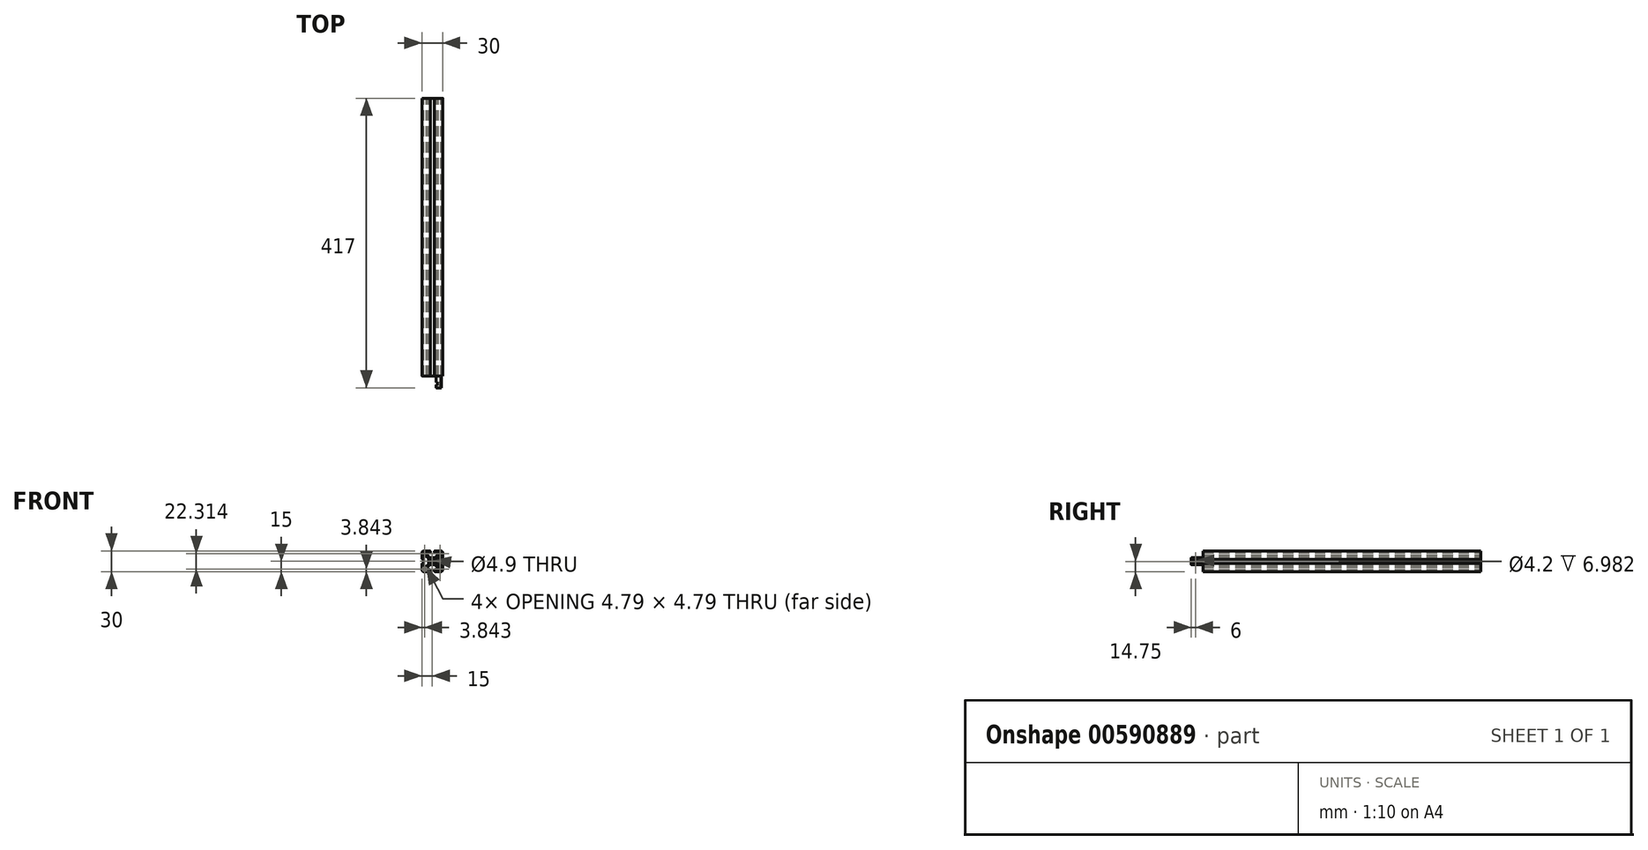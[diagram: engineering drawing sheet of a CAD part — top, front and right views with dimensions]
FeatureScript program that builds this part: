
annotation { "Feature Type Name" : "Feature", "Feature Type Description" : "" }
export const myFeature = defineFeature(function(context is Context, id is Id, definition is map)
    precondition{}
    {
        {
            var Q0;
            Q0=qCreatedBy(makeId("Front.planeOp"),FACE);
            var sketch = newSketch(context, id + "F0", { "sketchPlane" : qUnion([Q0])});
            skPoint(sketch, "E0.middle", {"position": v(0, 0) * mm});
            skCircle(sketch, "E1", {"center": v(0, 0) * mm, "radius": 2.45 * mm});
            skLineSegment(sketch, "E2", {"start": v(15, -15) * mm, "end": v(15, -3) * mm});
            skLineSegment(sketch, "E3", {"start": v(15, -3) * mm, "end": v(12.1, -3) * mm});
            skLineSegment(sketch, "E4", {"start": v(12.1, -3) * mm, "end": v(12.1, -5.9) * mm});
            skLineSegment(sketch, "E5", {"start": v(12.1, -5.9) * mm, "end": v(13.55, -5.9) * mm});
            skLineSegment(sketch, "E6", {"start": v(13.55, -5.9) * mm, "end": v(13.55, -7.35) * mm});
            skLineSegment(sketch, "E7", {"start": v(13.55, -7.35) * mm, "end": v(8.76, -7.35) * mm});
            skLineSegment(sketch, "E8", {"start": v(8.76, -7.35) * mm, "end": v(5.1, -3.69) * mm});
            skLineSegment(sketch, "E9", {"start": v(5.1, -3.69) * mm, "end": v(5.1, 0) * mm});
            skLineSegment(sketch, "E10", {"start": v(-37.03, 0) * mm, "end": v(41.88, 0) * mm, "construction": true});
            skLineSegment(sketch, "E11", {"start": v(0, 0) * mm, "end": v(18.28, -18.28) * mm, "construction": true});
            skLineSegment(sketch, "E12.MirrorCS", {"start": v(3.69, -5.1) * mm, "end": v(0, -5.1) * mm});
            skLineSegment(sketch, "E13.MirrorCS", {"start": v(7.35, -8.76) * mm, "end": v(3.69, -5.1) * mm});
            skLineSegment(sketch, "E14.MirrorCS", {"start": v(7.35, -13.55) * mm, "end": v(7.35, -8.76) * mm});
            skLineSegment(sketch, "E15.MirrorCS", {"start": v(5.9, -13.55) * mm, "end": v(7.35, -13.55) * mm});
            skLineSegment(sketch, "E16.MirrorCS", {"start": v(5.9, -12.1) * mm, "end": v(5.9, -13.55) * mm});
            skLineSegment(sketch, "E17.MirrorCS", {"start": v(3, -12.1) * mm, "end": v(5.9, -12.1) * mm});
            skLineSegment(sketch, "E18.MirrorCS", {"start": v(3, -15) * mm, "end": v(3, -12.1) * mm});
            skLineSegment(sketch, "E19.MirrorCS", {"start": v(15, -15) * mm, "end": v(3, -15) * mm});
            skLineSegment(sketch, "E20", {"start": v(0, 28.81) * mm, "end": v(0, -46.75) * mm, "construction": true});
            skLineSegment(sketch, "E21.MirrorCS", {"start": v(-5.1, -3.69) * mm, "end": v(-5.1, 0) * mm});
            skLineSegment(sketch, "E22.MirrorCS", {"start": v(-8.76, -7.35) * mm, "end": v(-5.1, -3.69) * mm});
            skLineSegment(sketch, "E23.MirrorCS", {"start": v(-13.55, -7.35) * mm, "end": v(-8.76, -7.35) * mm});
            skLineSegment(sketch, "E24.MirrorCS", {"start": v(-13.55, -5.9) * mm, "end": v(-13.55, -7.35) * mm});
            skLineSegment(sketch, "E25.MirrorCS", {"start": v(-12.1, -5.9) * mm, "end": v(-13.55, -5.9) * mm});
            skLineSegment(sketch, "E26.MirrorCS", {"start": v(-12.1, -3) * mm, "end": v(-12.1, -5.9) * mm});
            skLineSegment(sketch, "E27.MirrorCS", {"start": v(-15, -3) * mm, "end": v(-12.1, -3) * mm});
            skLineSegment(sketch, "E28.MirrorCS", {"start": v(-15, -15) * mm, "end": v(-15, -3) * mm});
            skLineSegment(sketch, "E29.MirrorCS", {"start": v(-15, -15) * mm, "end": v(-3, -15) * mm});
            skLineSegment(sketch, "E30.MirrorCS", {"start": v(-3, -15) * mm, "end": v(-3, -12.1) * mm});
            skLineSegment(sketch, "E31.MirrorCS", {"start": v(-3, -12.1) * mm, "end": v(-5.9, -12.1) * mm});
            skLineSegment(sketch, "E32.MirrorCS", {"start": v(-5.9, -13.55) * mm, "end": v(-7.35, -13.55) * mm});
            skLineSegment(sketch, "E33.MirrorCS", {"start": v(-7.35, -13.55) * mm, "end": v(-7.35, -8.76) * mm});
            skLineSegment(sketch, "E34.MirrorCS", {"start": v(-7.35, -8.76) * mm, "end": v(-3.69, -5.1) * mm});
            skLineSegment(sketch, "E35.MirrorCS", {"start": v(-3.69, -5.1) * mm, "end": v(0, -5.1) * mm});
            skLineSegment(sketch, "E36.MirrorCS", {"start": v(-5.9, -12.1) * mm, "end": v(-5.9, -13.55) * mm});
            skLineSegment(sketch, "E37.MirrorCS", {"start": v(-5.9, 13.55) * mm, "end": v(-7.35, 13.55) * mm});
            skLineSegment(sketch, "E38.MirrorCS", {"start": v(-13.55, 5.9) * mm, "end": v(-13.55, 7.35) * mm});
            skLineSegment(sketch, "E39.MirrorCS", {"start": v(-12.1, 5.9) * mm, "end": v(-13.55, 5.9) * mm});
            skLineSegment(sketch, "E40.MirrorCS", {"start": v(5.9, 12.1) * mm, "end": v(5.9, 13.55) * mm});
            skLineSegment(sketch, "E41.MirrorCS", {"start": v(5.9, 13.55) * mm, "end": v(7.35, 13.55) * mm});
            skLineSegment(sketch, "E42.MirrorCS", {"start": v(13.55, 5.9) * mm, "end": v(13.55, 7.35) * mm});
            skLineSegment(sketch, "E43.MirrorCS", {"start": v(-5.9, 12.1) * mm, "end": v(-5.9, 13.55) * mm});
            skLineSegment(sketch, "E44.MirrorCS", {"start": v(12.1, 5.9) * mm, "end": v(13.55, 5.9) * mm});
            skLineSegment(sketch, "E45.MirrorCS", {"start": v(12.1, 3) * mm, "end": v(12.1, 5.9) * mm});
            skLineSegment(sketch, "E46.MirrorCS", {"start": v(-7.35, 13.55) * mm, "end": v(-7.35, 8.76) * mm});
            skLineSegment(sketch, "E47.MirrorCS", {"start": v(3, 12.1) * mm, "end": v(5.9, 12.1) * mm});
            skLineSegment(sketch, "E48.MirrorCS", {"start": v(-3.69, 5.1) * mm, "end": v(0, 5.1) * mm});
            skLineSegment(sketch, "E49.MirrorCS", {"start": v(15, 15) * mm, "end": v(3, 15) * mm});
            skLineSegment(sketch, "E50.MirrorCS", {"start": v(-3, 15) * mm, "end": v(-3, 12.1) * mm});
            skLineSegment(sketch, "E51.MirrorCS", {"start": v(-13.55, 7.35) * mm, "end": v(-8.76, 7.35) * mm});
            skLineSegment(sketch, "E52.MirrorCS", {"start": v(-15, 15) * mm, "end": v(-3, 15) * mm});
            skLineSegment(sketch, "E53.MirrorCS", {"start": v(-15, 3) * mm, "end": v(-12.1, 3) * mm});
            skLineSegment(sketch, "E54.MirrorCS", {"start": v(-12.1, 3) * mm, "end": v(-12.1, 5.9) * mm});
            skLineSegment(sketch, "E55.MirrorCS", {"start": v(-15, 15) * mm, "end": v(-15, 3) * mm});
            skLineSegment(sketch, "E56.MirrorCS", {"start": v(-8.76, 7.35) * mm, "end": v(-5.1, 3.69) * mm});
            skLineSegment(sketch, "E57.MirrorCS", {"start": v(7.35, 8.76) * mm, "end": v(3.69, 5.1) * mm});
            skLineSegment(sketch, "E58.MirrorCS", {"start": v(-7.35, 8.76) * mm, "end": v(-3.69, 5.1) * mm});
            skLineSegment(sketch, "E59.MirrorCS", {"start": v(-3, 12.1) * mm, "end": v(-5.9, 12.1) * mm});
            skLineSegment(sketch, "E60.MirrorCS", {"start": v(15, 15) * mm, "end": v(15, 3) * mm});
            skLineSegment(sketch, "E61.MirrorCS", {"start": v(3.69, 5.1) * mm, "end": v(0, 5.1) * mm});
            skLineSegment(sketch, "E62.MirrorCS", {"start": v(3, 15) * mm, "end": v(3, 12.1) * mm});
            skLineSegment(sketch, "E63.MirrorCS", {"start": v(15, 3) * mm, "end": v(12.1, 3) * mm});
            skLineSegment(sketch, "E64.MirrorCS", {"start": v(8.76, 7.35) * mm, "end": v(5.1, 3.69) * mm});
            skLineSegment(sketch, "E65.MirrorCS", {"start": v(7.35, 13.55) * mm, "end": v(7.35, 8.76) * mm});
            skLineSegment(sketch, "E66.MirrorCS", {"start": v(13.55, 7.35) * mm, "end": v(8.76, 7.35) * mm});
            skLineSegment(sketch, "E67.MirrorCS", {"start": v(-5.1, 3.69) * mm, "end": v(-5.1, 0) * mm});
            skLineSegment(sketch, "E68.MirrorCS", {"start": v(5.1, 3.69) * mm, "end": v(5.1, 0) * mm});
            skLineSegment(sketch, "E69", {"start": v(13.55, -13.55) * mm, "end": v(13.55, -8.76) * mm});
            skLineSegment(sketch, "E70", {"start": v(13.55, -8.76) * mm, "end": v(8.76, -8.76) * mm});
            skLineSegment(sketch, "E71.MirrorCS", {"start": v(8.76, -13.55) * mm, "end": v(8.76, -8.76) * mm});
            skLineSegment(sketch, "E72.MirrorCS", {"start": v(13.55, -13.55) * mm, "end": v(8.76, -13.55) * mm});
            skLineSegment(sketch, "E73.MirrorCS", {"start": v(-13.55, -8.76) * mm, "end": v(-8.76, -8.76) * mm});
            skLineSegment(sketch, "E74.MirrorCS", {"start": v(-13.55, -13.55) * mm, "end": v(-13.55, -8.76) * mm});
            skLineSegment(sketch, "E75.MirrorCS", {"start": v(-13.55, -13.55) * mm, "end": v(-8.76, -13.55) * mm});
            skLineSegment(sketch, "E76.MirrorCS", {"start": v(-8.76, -13.55) * mm, "end": v(-8.76, -8.76) * mm});
            skLineSegment(sketch, "E77.MirrorCS", {"start": v(-13.55, 8.76) * mm, "end": v(-8.76, 8.76) * mm});
            skLineSegment(sketch, "E78.MirrorCS", {"start": v(-13.55, 13.55) * mm, "end": v(-13.55, 8.76) * mm});
            skLineSegment(sketch, "E79.MirrorCS", {"start": v(-8.76, 13.55) * mm, "end": v(-8.76, 8.76) * mm});
            skLineSegment(sketch, "E80.MirrorCS", {"start": v(-13.55, 13.55) * mm, "end": v(-8.76, 13.55) * mm});
            skLineSegment(sketch, "E81.MirrorCS", {"start": v(13.55, 8.76) * mm, "end": v(8.76, 8.76) * mm});
            skLineSegment(sketch, "E82.MirrorCS", {"start": v(8.76, 13.55) * mm, "end": v(8.76, 8.76) * mm});
            skLineSegment(sketch, "E83.MirrorCS", {"start": v(13.55, 13.55) * mm, "end": v(8.76, 13.55) * mm});
            skLineSegment(sketch, "E84.MirrorCS", {"start": v(13.55, 13.55) * mm, "end": v(13.55, 8.76) * mm});
            skSolve(sketch);
        }
        {
            var Q0;
            Q0=makeQuery(id+"F0.imprint","IMPRINT",FACE,{"disambiguationData":[TD([[makeQuery(id+"F0.imprint","IMPRINT",EDGE,{"derivedFrom":sQuery(id+"F0.wireOp",EDGE,"E1")}),-1.0]])]});
            extrude(context, id + "F1", {"entities" : qUnion([Q0]), "depth" : 400 * mm, "offsetDistance" : 25 * mm});
        }
        {
            var Q0;
            Q0=makeQuery(id+"F1.opExtrude","SWEPT_EDGE",EDGE,{"disambiguationData":[OSD([sQuery(id+"F0.wireOp",EDGE,"E3"),sQuery(id+"F0.wireOp",EDGE,"E4")])]});
            var Q1;
            Q1=makeQuery(id+"F1.opExtrude","SWEPT_EDGE",EDGE,{"disambiguationData":[OSD([sQuery(id+"F0.wireOp",EDGE,"E2"),sQuery(id+"F0.wireOp",EDGE,"E3")])]});
            var Q2;
            Q2=makeQuery(id+"F1.opExtrude","SWEPT_EDGE",EDGE,{"disambiguationData":[OSD([sQuery(id+"F0.wireOp",EDGE,"E45.MirrorCS"),sQuery(id+"F0.wireOp",EDGE,"E63.MirrorCS")])]});
            var Q3;
            Q3=makeQuery(id+"F1.opExtrude","SWEPT_EDGE",EDGE,{"disambiguationData":[OSD([sQuery(id+"F0.wireOp",EDGE,"E60.MirrorCS"),sQuery(id+"F0.wireOp",EDGE,"E63.MirrorCS")])]});
            var Q4;
            Q4=makeQuery(id+"F1.opExtrude","SWEPT_EDGE",EDGE,{"disambiguationData":[OSD([sQuery(id+"F0.wireOp",EDGE,"E18.MirrorCS"),sQuery(id+"F0.wireOp",EDGE,"E19.MirrorCS")])]});
            var Q5;
            Q5=makeQuery(id+"F1.opExtrude","SWEPT_EDGE",EDGE,{"disambiguationData":[OSD([sQuery(id+"F0.wireOp",EDGE,"E17.MirrorCS"),sQuery(id+"F0.wireOp",EDGE,"E18.MirrorCS")])]});
            var Q6;
            Q6=makeQuery(id+"F1.opExtrude","SWEPT_EDGE",EDGE,{"disambiguationData":[OSD([sQuery(id+"F0.wireOp",EDGE,"E29.MirrorCS"),sQuery(id+"F0.wireOp",EDGE,"E30.MirrorCS")])]});
            var Q7;
            Q7=makeQuery(id+"F1.opExtrude","SWEPT_EDGE",EDGE,{"disambiguationData":[OSD([sQuery(id+"F0.wireOp",EDGE,"E30.MirrorCS"),sQuery(id+"F0.wireOp",EDGE,"E31.MirrorCS")])]});
            var Q8;
            Q8=makeQuery(id+"F1.opExtrude","SWEPT_EDGE",EDGE,{"disambiguationData":[OSD([sQuery(id+"F0.wireOp",EDGE,"E27.MirrorCS"),sQuery(id+"F0.wireOp",EDGE,"E28.MirrorCS")])]});
            var Q9;
            Q9=makeQuery(id+"F1.opExtrude","SWEPT_EDGE",EDGE,{"disambiguationData":[OSD([sQuery(id+"F0.wireOp",EDGE,"E26.MirrorCS"),sQuery(id+"F0.wireOp",EDGE,"E27.MirrorCS")])]});
            var Q10;
            Q10=makeQuery(id+"F1.opExtrude","SWEPT_EDGE",EDGE,{"disambiguationData":[OSD([sQuery(id+"F0.wireOp",EDGE,"E53.MirrorCS"),sQuery(id+"F0.wireOp",EDGE,"E54.MirrorCS")])]});
            var Q11;
            Q11=makeQuery(id+"F1.opExtrude","SWEPT_EDGE",EDGE,{"disambiguationData":[OSD([sQuery(id+"F0.wireOp",EDGE,"E53.MirrorCS"),sQuery(id+"F0.wireOp",EDGE,"E55.MirrorCS")])]});
            var Q12;
            Q12=makeQuery(id+"F1.opExtrude","SWEPT_EDGE",EDGE,{"disambiguationData":[OSD([sQuery(id+"F0.wireOp",EDGE,"E50.MirrorCS"),sQuery(id+"F0.wireOp",EDGE,"E59.MirrorCS")])]});
            var Q13;
            Q13=makeQuery(id+"F1.opExtrude","SWEPT_EDGE",EDGE,{"disambiguationData":[OSD([sQuery(id+"F0.wireOp",EDGE,"E50.MirrorCS"),sQuery(id+"F0.wireOp",EDGE,"E52.MirrorCS")])]});
            var Q14;
            Q14=makeQuery(id+"F1.opExtrude","SWEPT_EDGE",EDGE,{"disambiguationData":[OSD([sQuery(id+"F0.wireOp",EDGE,"E47.MirrorCS"),sQuery(id+"F0.wireOp",EDGE,"E62.MirrorCS")])]});
            var Q15;
            Q15=makeQuery(id+"F1.opExtrude","SWEPT_EDGE",EDGE,{"disambiguationData":[OSD([sQuery(id+"F0.wireOp",EDGE,"E49.MirrorCS"),sQuery(id+"F0.wireOp",EDGE,"E62.MirrorCS")])]});
            var Q16;
            Q16=makeQuery(id+"F1.opExtrude","SWEPT_EDGE",EDGE,{"disambiguationData":[OSD([sQuery(id+"F0.wireOp",EDGE,"E38.MirrorCS"),sQuery(id+"F0.wireOp",EDGE,"E51.MirrorCS")])]});
            var Q17;
            Q17=makeQuery(id+"F1.opExtrude","SWEPT_EDGE",EDGE,{"disambiguationData":[OSD([sQuery(id+"F0.wireOp",EDGE,"E37.MirrorCS"),sQuery(id+"F0.wireOp",EDGE,"E46.MirrorCS")])]});
            var Q18;
            Q18=makeQuery(id+"F1.opExtrude","SWEPT_EDGE",EDGE,{"disambiguationData":[OSD([sQuery(id+"F0.wireOp",EDGE,"E41.MirrorCS"),sQuery(id+"F0.wireOp",EDGE,"E65.MirrorCS")])]});
            var Q19;
            Q19=makeQuery(id+"F1.opExtrude","SWEPT_EDGE",EDGE,{"disambiguationData":[OSD([sQuery(id+"F0.wireOp",EDGE,"E42.MirrorCS"),sQuery(id+"F0.wireOp",EDGE,"E66.MirrorCS")])]});
            var Q20;
            Q20=makeQuery(id+"F1.opExtrude","SWEPT_EDGE",EDGE,{"disambiguationData":[OSD([sQuery(id+"F0.wireOp",EDGE,"E14.MirrorCS"),sQuery(id+"F0.wireOp",EDGE,"E15.MirrorCS")])]});
            var Q21;
            Q21=makeQuery(id+"F1.opExtrude","SWEPT_EDGE",EDGE,{"disambiguationData":[OSD([sQuery(id+"F0.wireOp",EDGE,"E6"),sQuery(id+"F0.wireOp",EDGE,"E7")])]});
            var Q22;
            Q22=makeQuery(id+"F1.opExtrude","SWEPT_EDGE",EDGE,{"disambiguationData":[OSD([sQuery(id+"F0.wireOp",EDGE,"E32.MirrorCS"),sQuery(id+"F0.wireOp",EDGE,"E33.MirrorCS")])]});
            var Q23;
            Q23=makeQuery(id+"F1.opExtrude","SWEPT_EDGE",EDGE,{"disambiguationData":[OSD([sQuery(id+"F0.wireOp",EDGE,"E23.MirrorCS"),sQuery(id+"F0.wireOp",EDGE,"E24.MirrorCS")])]});
            fillet(context, id + "F2", {"entities" : qUnion([Q0, Q1, Q2, Q3, Q4, Q5, Q6, Q7, Q8, Q9, Q10, Q11, Q12, Q13, Q14, Q15, Q16, Q17, Q18, Q19, Q20, Q21, Q22, Q23]), "radius" : 1 * mm, "tangentPropagation" : true, "allowEdgeOverflow" : false});
        }
        {
            var Q0;
            Q0=makeQuery(id+"F1.opExtrude","SWEPT_EDGE",EDGE,{"disambiguationData":[OSD([sQuery(id+"F0.wireOp",EDGE,"E49.MirrorCS"),sQuery(id+"F0.wireOp",EDGE,"E60.MirrorCS")])]});
            var Q1;
            Q1=makeQuery(id+"F1.opExtrude","SWEPT_EDGE",EDGE,{"disambiguationData":[OSD([sQuery(id+"F0.wireOp",EDGE,"E52.MirrorCS"),sQuery(id+"F0.wireOp",EDGE,"E55.MirrorCS")])]});
            var Q2;
            Q2=makeQuery(id+"F1.opExtrude","SWEPT_EDGE",EDGE,{"disambiguationData":[OSD([sQuery(id+"F0.wireOp",EDGE,"E28.MirrorCS"),sQuery(id+"F0.wireOp",EDGE,"E29.MirrorCS")])]});
            var Q3;
            Q3=makeQuery(id+"F1.opExtrude","SWEPT_EDGE",EDGE,{"disambiguationData":[OSD([sQuery(id+"F0.wireOp",EDGE,"E2"),sQuery(id+"F0.wireOp",EDGE,"E19.MirrorCS")])]});
            fillet(context, id + "F3", {"entities" : qUnion([Q0, Q1, Q2, Q3]), "radius" : 2.9 * mm, "tangentPropagation" : true, "allowEdgeOverflow" : false});
        }
        {
            var Q0;
            Q0=makeQuery(id+"F1.opExtrude","SWEPT_EDGE",EDGE,{"disambiguationData":[OSD([sQuery(id+"F0.wireOp",EDGE,"E69"),sQuery(id+"F0.wireOp",EDGE,"E72.MirrorCS")])]});
            var Q1;
            Q1=makeQuery(id+"F1.opExtrude","SWEPT_EDGE",EDGE,{"disambiguationData":[OSD([sQuery(id+"F0.wireOp",EDGE,"E74.MirrorCS"),sQuery(id+"F0.wireOp",EDGE,"E75.MirrorCS")])]});
            var Q2;
            Q2=makeQuery(id+"F1.opExtrude","SWEPT_EDGE",EDGE,{"disambiguationData":[OSD([sQuery(id+"F0.wireOp",EDGE,"E78.MirrorCS"),sQuery(id+"F0.wireOp",EDGE,"E80.MirrorCS")])]});
            var Q3;
            Q3=makeQuery(id+"F1.opExtrude","SWEPT_EDGE",EDGE,{"disambiguationData":[OSD([sQuery(id+"F0.wireOp",EDGE,"E83.MirrorCS"),sQuery(id+"F0.wireOp",EDGE,"E84.MirrorCS")])]});
            var Q4;
            Q4=makeQuery(id+"F1.opExtrude","SWEPT_EDGE",EDGE,{"disambiguationData":[OSD([sQuery(id+"F0.wireOp",EDGE,"E33.MirrorCS"),sQuery(id+"F0.wireOp",EDGE,"E34.MirrorCS")])]});
            var Q5;
            Q5=makeQuery(id+"F1.opExtrude","SWEPT_EDGE",EDGE,{"disambiguationData":[OSD([sQuery(id+"F0.wireOp",EDGE,"E34.MirrorCS"),sQuery(id+"F0.wireOp",EDGE,"E35.MirrorCS")])]});
            var Q6;
            Q6=makeQuery(id+"F1.opExtrude","SWEPT_EDGE",EDGE,{"disambiguationData":[OSD([sQuery(id+"F0.wireOp",EDGE,"E12.MirrorCS"),sQuery(id+"F0.wireOp",EDGE,"E13.MirrorCS")])]});
            var Q7;
            Q7=makeQuery(id+"F1.opExtrude","SWEPT_EDGE",EDGE,{"disambiguationData":[OSD([sQuery(id+"F0.wireOp",EDGE,"E13.MirrorCS"),sQuery(id+"F0.wireOp",EDGE,"E14.MirrorCS")])]});
            var Q8;
            Q8=makeQuery(id+"F1.opExtrude","SWEPT_EDGE",EDGE,{"disambiguationData":[OSD([sQuery(id+"F0.wireOp",EDGE,"E7"),sQuery(id+"F0.wireOp",EDGE,"E8")])]});
            var Q9;
            Q9=makeQuery(id+"F1.opExtrude","SWEPT_EDGE",EDGE,{"disambiguationData":[OSD([sQuery(id+"F0.wireOp",EDGE,"E8"),sQuery(id+"F0.wireOp",EDGE,"E9")])]});
            var Q10;
            Q10=makeQuery(id+"F1.opExtrude","SWEPT_EDGE",EDGE,{"disambiguationData":[OSD([sQuery(id+"F0.wireOp",EDGE,"E64.MirrorCS"),sQuery(id+"F0.wireOp",EDGE,"E68.MirrorCS")])]});
            var Q11;
            Q11=makeQuery(id+"F1.opExtrude","SWEPT_EDGE",EDGE,{"disambiguationData":[OSD([sQuery(id+"F0.wireOp",EDGE,"E64.MirrorCS"),sQuery(id+"F0.wireOp",EDGE,"E66.MirrorCS")])]});
            var Q12;
            Q12=makeQuery(id+"F1.opExtrude","SWEPT_EDGE",EDGE,{"disambiguationData":[OSD([sQuery(id+"F0.wireOp",EDGE,"E46.MirrorCS"),sQuery(id+"F0.wireOp",EDGE,"E58.MirrorCS")])]});
            var Q13;
            Q13=makeQuery(id+"F1.opExtrude","SWEPT_EDGE",EDGE,{"disambiguationData":[OSD([sQuery(id+"F0.wireOp",EDGE,"E48.MirrorCS"),sQuery(id+"F0.wireOp",EDGE,"E58.MirrorCS")])]});
            var Q14;
            Q14=makeQuery(id+"F1.opExtrude","SWEPT_EDGE",EDGE,{"disambiguationData":[OSD([sQuery(id+"F0.wireOp",EDGE,"E57.MirrorCS"),sQuery(id+"F0.wireOp",EDGE,"E61.MirrorCS")])]});
            var Q15;
            Q15=makeQuery(id+"F1.opExtrude","SWEPT_EDGE",EDGE,{"disambiguationData":[OSD([sQuery(id+"F0.wireOp",EDGE,"E57.MirrorCS"),sQuery(id+"F0.wireOp",EDGE,"E65.MirrorCS")])]});
            var Q16;
            Q16=makeQuery(id+"F1.opExtrude","SWEPT_EDGE",EDGE,{"disambiguationData":[OSD([sQuery(id+"F0.wireOp",EDGE,"E51.MirrorCS"),sQuery(id+"F0.wireOp",EDGE,"E56.MirrorCS")])]});
            var Q17;
            Q17=makeQuery(id+"F1.opExtrude","SWEPT_EDGE",EDGE,{"disambiguationData":[OSD([sQuery(id+"F0.wireOp",EDGE,"E56.MirrorCS"),sQuery(id+"F0.wireOp",EDGE,"E67.MirrorCS")])]});
            var Q18;
            Q18=makeQuery(id+"F1.opExtrude","SWEPT_EDGE",EDGE,{"disambiguationData":[OSD([sQuery(id+"F0.wireOp",EDGE,"E21.MirrorCS"),sQuery(id+"F0.wireOp",EDGE,"E22.MirrorCS")])]});
            var Q19;
            Q19=makeQuery(id+"F1.opExtrude","SWEPT_EDGE",EDGE,{"disambiguationData":[OSD([sQuery(id+"F0.wireOp",EDGE,"E22.MirrorCS"),sQuery(id+"F0.wireOp",EDGE,"E23.MirrorCS")])]});
            fillet(context, id + "F4", {"entities" : qUnion([Q0, Q1, Q2, Q3, Q4, Q5, Q6, Q7, Q8, Q9, Q10, Q11, Q12, Q13, Q14, Q15, Q16, Q17, Q18, Q19]), "radius" : 1.45 * mm, "tangentPropagation" : true, "allowEdgeOverflow" : false});
        }
        {
            var Q0;
            Q0=makeQuery(id+"F1.opExtrude","CAP_FACE",FACE,{"disambiguationData":[OSD([sQuery(id+"F0.wireOp",EDGE,"E1"),sQuery(id+"F0.wireOp",EDGE,"E2"),sQuery(id+"F0.wireOp",EDGE,"E3"),sQuery(id+"F0.wireOp",EDGE,"E4"),sQuery(id+"F0.wireOp",EDGE,"E5"),sQuery(id+"F0.wireOp",EDGE,"E6"),sQuery(id+"F0.wireOp",EDGE,"E7"),sQuery(id+"F0.wireOp",EDGE,"E8"),sQuery(id+"F0.wireOp",EDGE,"E9"),sQuery(id+"F0.wireOp",EDGE,"E12.MirrorCS"),sQuery(id+"F0.wireOp",EDGE,"E13.MirrorCS"),sQuery(id+"F0.wireOp",EDGE,"E14.MirrorCS"),sQuery(id+"F0.wireOp",EDGE,"E15.MirrorCS"),sQuery(id+"F0.wireOp",EDGE,"E16.MirrorCS"),sQuery(id+"F0.wireOp",EDGE,"E17.MirrorCS"),sQuery(id+"F0.wireOp",EDGE,"E18.MirrorCS"),sQuery(id+"F0.wireOp",EDGE,"E19.MirrorCS"),sQuery(id+"F0.wireOp",EDGE,"E21.MirrorCS"),sQuery(id+"F0.wireOp",EDGE,"E22.MirrorCS"),sQuery(id+"F0.wireOp",EDGE,"E23.MirrorCS"),sQuery(id+"F0.wireOp",EDGE,"E24.MirrorCS"),sQuery(id+"F0.wireOp",EDGE,"E25.MirrorCS"),sQuery(id+"F0.wireOp",EDGE,"E26.MirrorCS"),sQuery(id+"F0.wireOp",EDGE,"E27.MirrorCS"),sQuery(id+"F0.wireOp",EDGE,"E28.MirrorCS"),sQuery(id+"F0.wireOp",EDGE,"E29.MirrorCS"),sQuery(id+"F0.wireOp",EDGE,"E30.MirrorCS"),sQuery(id+"F0.wireOp",EDGE,"E31.MirrorCS"),sQuery(id+"F0.wireOp",EDGE,"E32.MirrorCS"),sQuery(id+"F0.wireOp",EDGE,"E33.MirrorCS"),sQuery(id+"F0.wireOp",EDGE,"E34.MirrorCS"),sQuery(id+"F0.wireOp",EDGE,"E35.MirrorCS"),sQuery(id+"F0.wireOp",EDGE,"E36.MirrorCS"),sQuery(id+"F0.wireOp",EDGE,"E37.MirrorCS"),sQuery(id+"F0.wireOp",EDGE,"E38.MirrorCS"),sQuery(id+"F0.wireOp",EDGE,"E39.MirrorCS"),sQuery(id+"F0.wireOp",EDGE,"E40.MirrorCS"),sQuery(id+"F0.wireOp",EDGE,"E41.MirrorCS"),sQuery(id+"F0.wireOp",EDGE,"E42.MirrorCS"),sQuery(id+"F0.wireOp",EDGE,"E43.MirrorCS"),sQuery(id+"F0.wireOp",EDGE,"E44.MirrorCS"),sQuery(id+"F0.wireOp",EDGE,"E45.MirrorCS"),sQuery(id+"F0.wireOp",EDGE,"E46.MirrorCS"),sQuery(id+"F0.wireOp",EDGE,"E47.MirrorCS"),sQuery(id+"F0.wireOp",EDGE,"E48.MirrorCS"),sQuery(id+"F0.wireOp",EDGE,"E49.MirrorCS"),sQuery(id+"F0.wireOp",EDGE,"E50.MirrorCS"),sQuery(id+"F0.wireOp",EDGE,"E51.MirrorCS"),sQuery(id+"F0.wireOp",EDGE,"E52.MirrorCS"),sQuery(id+"F0.wireOp",EDGE,"E53.MirrorCS"),sQuery(id+"F0.wireOp",EDGE,"E54.MirrorCS"),sQuery(id+"F0.wireOp",EDGE,"E55.MirrorCS"),sQuery(id+"F0.wireOp",EDGE,"E56.MirrorCS"),sQuery(id+"F0.wireOp",EDGE,"E57.MirrorCS"),sQuery(id+"F0.wireOp",EDGE,"E58.MirrorCS"),sQuery(id+"F0.wireOp",EDGE,"E59.MirrorCS"),sQuery(id+"F0.wireOp",EDGE,"E60.MirrorCS"),sQuery(id+"F0.wireOp",EDGE,"E61.MirrorCS"),sQuery(id+"F0.wireOp",EDGE,"E62.MirrorCS"),sQuery(id+"F0.wireOp",EDGE,"E63.MirrorCS"),sQuery(id+"F0.wireOp",EDGE,"E64.MirrorCS"),sQuery(id+"F0.wireOp",EDGE,"E65.MirrorCS"),sQuery(id+"F0.wireOp",EDGE,"E66.MirrorCS"),sQuery(id+"F0.wireOp",EDGE,"E67.MirrorCS"),sQuery(id+"F0.wireOp",EDGE,"E68.MirrorCS"),sQuery(id+"F0.wireOp",EDGE,"E69"),sQuery(id+"F0.wireOp",EDGE,"E70"),sQuery(id+"F0.wireOp",EDGE,"E71.MirrorCS"),sQuery(id+"F0.wireOp",EDGE,"E72.MirrorCS"),sQuery(id+"F0.wireOp",EDGE,"E73.MirrorCS"),sQuery(id+"F0.wireOp",EDGE,"E74.MirrorCS"),sQuery(id+"F0.wireOp",EDGE,"E75.MirrorCS"),sQuery(id+"F0.wireOp",EDGE,"E76.MirrorCS"),sQuery(id+"F0.wireOp",EDGE,"E77.MirrorCS"),sQuery(id+"F0.wireOp",EDGE,"E78.MirrorCS"),sQuery(id+"F0.wireOp",EDGE,"E79.MirrorCS"),sQuery(id+"F0.wireOp",EDGE,"E80.MirrorCS"),sQuery(id+"F0.wireOp",EDGE,"E81.MirrorCS"),sQuery(id+"F0.wireOp",EDGE,"E82.MirrorCS"),sQuery(id+"F0.wireOp",EDGE,"E83.MirrorCS"),sQuery(id+"F0.wireOp",EDGE,"E84.MirrorCS")])],"isStart":false});
            var sketch = newSketch(context, id + "F5", { "sketchPlane" : qUnion([Q0])});
            skLineSegment(sketch, "E85", {"start": v(12.1, 3) * mm, "end": v(12.1, 5.25) * mm});
            skLineSegment(sketch, "E86", {"start": v(12.1, 3) * mm, "end": v(13.1, 3) * mm});
            skLineSegment(sketch, "E87", {"start": v(0, 0) * mm, "end": v(28.03, 0) * mm, "construction": true});
            skLineSegment(sketch, "E88.MirrorCS", {"start": v(12.1, -3) * mm, "end": v(13.1, -3) * mm});
            skLineSegment(sketch, "E89.MirrorCS", {"start": v(12.1, -3) * mm, "end": v(12.1, -5.25) * mm});
            skPoint(sketch, "E90", {"position": v(12.1, 0) * mm});
            skArc(sketch, "E91", {"start": v(13.1, 3) * mm, "mid": v(12.1, 0) * mm, "end": v(13.1, -3) * mm});
            skLineSegment(sketch, "E92", {"start": v(12.1, 5.25) * mm, "end": v(5.3, 0) * mm});
            skLineSegment(sketch, "E93.MirrorCS", {"start": v(12.1, -5.25) * mm, "end": v(5.3, 0) * mm});
            skSolve(sketch);
        }
        {
            var Q0;
            {var subQ0=sQuery(id+"F5.wireOp",EDGE,"E91");var subQ1=sQuery(id+"F5.wireOp",EDGE,"E86");var subQ2=makeQuery(id+"F5.imprint","INTERSECT",VERTEX,{"derivedFrom":[subQ1,subQ0]});Q0=makeQuery(id+"F5.imprint","IMPRINT",FACE,{"disambiguationData":[TD([[makeQuery(id+"F5.imprint","IMPRINT",EDGE,{"disambiguationData":[TD([[subQ2,1.0]])],"derivedFrom":subQ1}),-1.0]])]});}
            var Q1;
            {var subQ0=sQuery(id+"F5.wireOp",EDGE,"E91");var subQ1=sQuery(id+"F5.wireOp",EDGE,"E88.MirrorCS");var subQ2=makeQuery(id+"F5.imprint","INTERSECT",VERTEX,{"derivedFrom":[subQ1,subQ0]});Q1=makeQuery(id+"F5.imprint","IMPRINT",FACE,{"disambiguationData":[TD([[makeQuery(id+"F5.imprint","IMPRINT",EDGE,{"disambiguationData":[TD([[subQ2,1.0]])],"derivedFrom":subQ1}),1.0]])]});}
            var Q2;
            {var subQ10=sQuery(id+"F5.wireOp",EDGE,"E85");Q2=makeQuery(id+"F5.imprint","IMPRINT",FACE,{"disambiguationData":[TD([[makeQuery(id+"F5.imprint","IMPRINT",EDGE,{"derivedFrom":subQ10}),1.0]])]});}
            extrude(context, id + "F6", {"entities" : qUnion([Q0, Q1, Q2]), "depth" : 17 * mm, "offsetDistance" : 25 * mm});
        }
        {
            var Q0;
            Q0=makeQuery(id+"F6.opExtrude","SWEPT_EDGE",EDGE,{"disambiguationData":[OSD([sQuery(id+"F5.wireOp",EDGE,"E92"),sQuery(id+"F5.wireOp",EDGE,"E93.MirrorCS")])]});
            fillet(context, id + "F7", {"entities" : qUnion([Q0]), "radius" : 0.5 * mm, "tangentPropagation" : true, "allowEdgeOverflow" : false});
        }
        {
            var Q0;
            Q0=makeQuery(id+"F6.opExtrude","SWEPT_EDGE",EDGE,{"disambiguationData":[OSD([sQuery(id+"F5.wireOp",EDGE,"E85"),sQuery(id+"F5.wireOp",EDGE,"E92")])]});
            var Q1;
            Q1=makeQuery(id+"F6.opExtrude","SWEPT_EDGE",EDGE,{"disambiguationData":[OSD([sQuery(id+"F5.wireOp",EDGE,"E89.MirrorCS"),sQuery(id+"F5.wireOp",EDGE,"E93.MirrorCS")])]});
            fillet(context, id + "F8", {"entities" : qUnion([Q0, Q1]), "radius" : 0.3 * mm, "tangentPropagation" : true, "allowEdgeOverflow" : false});
        }
        {
            var Q0;
            Q0=makeQuery(id+"F6.opExtrude","SWEPT_FACE",FACE,{"disambiguationData":[OSD([sQuery(id+"F5.wireOp",EDGE,"E85")])]});
            cPlane(context, id + "F9", {"entities" : qUnion([Q0]), "cplaneType" : CPlaneType.OFFSET, "offset" : 0.5 * mm, "width" : 150 * mm, "height" : 150 * mm});
        }
        {
            var Q0;
            Q0=qCreatedBy(id+"F9.planeOp",FACE);
            var sketch = newSketch(context, id + "F10", { "sketchPlane" : qUnion([Q0])});
            skCircle(sketch, "E94", {"center": v(-411, -0.25) * mm, "radius": 2.25 * mm});
            skSolve(sketch);
        }
        {
            var Q0;
            Q0=sQuery(id+"F10.wireOp",VERTEX,"E94.center");
            var Q1;
            Q1=makeQuery(id+"F6.opExtrude","SWEPT_BODY",BODY,{"disambiguationData":[OSD([sQuery(id+"F5.wireOp",EDGE,"E85"),sQuery(id+"F5.wireOp",EDGE,"E86"),sQuery(id+"F5.wireOp",EDGE,"E88.MirrorCS"),sQuery(id+"F5.wireOp",EDGE,"E89.MirrorCS"),sQuery(id+"F5.wireOp",EDGE,"E91"),sQuery(id+"F5.wireOp",EDGE,"E92"),sQuery(id+"F5.wireOp",EDGE,"E93.MirrorCS")])]});
            hole(context, id + "F11", {"style" : HoleStyle.SIMPLE, "endStyle" : HoleEndStyle.THROUGH, "standardTappedOrClearance" : lookupTablePath({ "standard" : "ISO", "engagement" : "75%", "pitch" : "0.8 mm", "size" : "M5", "type" : "Tapped" }), "standardBlindInLast" : lookupTablePath({ "standard" : "ISO", "engagement" : "75%", "pitch" : "0.8 mm", "size" : "M5", "type" : "Tapped" }), "holeDiameter" : 4.2 * mm, "majorDiameter" : 5 * mm, "showTappedDepth" : true, "isTappedThrough" : true, "tappedDepth" : 12 * mm, "tapClearance" : 3, "locations" : qUnion([Q0]), "scope" : qUnion([Q1])});
        }
    });
